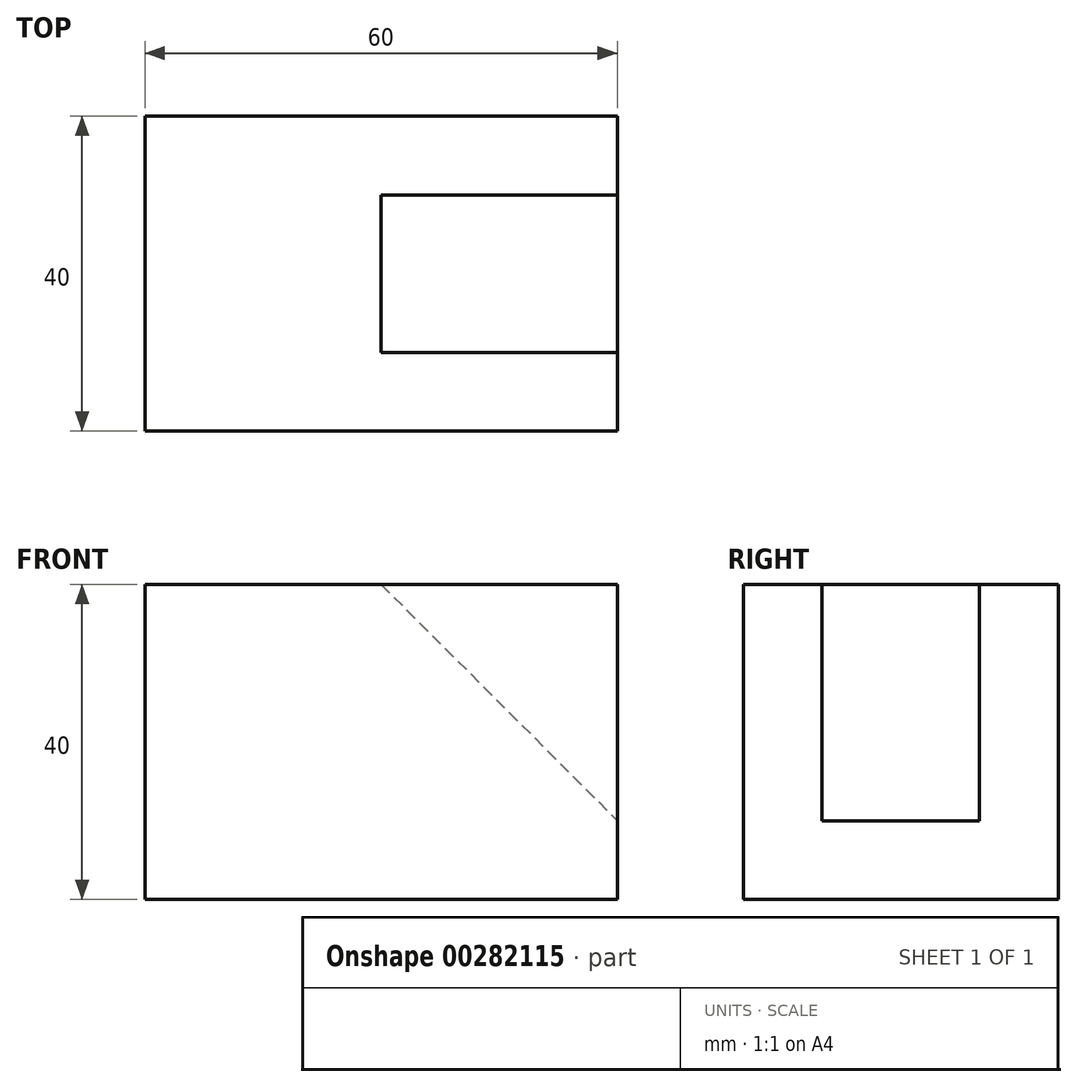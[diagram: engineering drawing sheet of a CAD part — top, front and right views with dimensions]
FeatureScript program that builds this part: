
annotation { "Feature Type Name" : "Feature", "Feature Type Description" : "" }
export const myFeature = defineFeature(function(context is Context, id is Id, definition is map)
    precondition{}
    {
        {
            var Q0;
            Q0=qCreatedBy(makeId("Front.planeOp"),FACE);
            var sketch = newSketch(context, id + "F0", { "sketchPlane" : qUnion([Q0])});
            skLineSegment(sketch, "E0", {"start": v(39.64, 0) * mm, "end": v(39.64, 10) * mm});
            skLineSegment(sketch, "E1", {"start": v(39.64, 10) * mm, "end": v(9.64, 40) * mm});
            skLineSegment(sketch, "E2", {"start": v(9.64, 40) * mm, "end": v(-20.36, 40) * mm});
            skLineSegment(sketch, "E3", {"start": v(-20.36, 40) * mm, "end": v(-20.36, 0) * mm});
            skLineSegment(sketch, "E4", {"start": v(-20.36, 0) * mm, "end": v(39.64, 0) * mm});
            skSolve(sketch);
        }
        {
            var Q0;
            Q0 = qSketchRegion(id + "F0", true);
            extrude(context, id + "F1", {"entities" : qUnion([Q0]), "oppositeDirection" : true, "depth" : 40 * mm});
        }
        {
            var Q0;
            Q0=makeQuery(id+"F1.opExtrude","SWEPT_FACE",FACE,{"disambiguationData":[OSD([sQuery(id+"F0.wireOp",EDGE,"E4")])]});
            var sketch = newSketch(context, id + "F2", { "sketchPlane" : qUnion([Q0])});
            skLineSegment(sketch, "E5", {"start": v(39.64, 0) * mm, "end": v(39.64, -10) * mm});
            skLineSegment(sketch, "E6", {"start": v(39.64, -10) * mm, "end": v(9.64, -10) * mm});
            skLineSegment(sketch, "E7", {"start": v(9.64, -10) * mm, "end": v(9.64, -30) * mm});
            skLineSegment(sketch, "E8", {"start": v(9.64, -30) * mm, "end": v(39.64, -30) * mm});
            skLineSegment(sketch, "E9", {"start": v(39.64, -30) * mm, "end": v(39.64, -40) * mm});
            skLineSegment(sketch, "E10", {"start": v(39.64, -40) * mm, "end": v(2.8, -40) * mm});
            skLineSegment(sketch, "E11", {"start": v(2.8, -40) * mm, "end": v(2.8, 0) * mm});
            skLineSegment(sketch, "E12", {"start": v(2.8, 0) * mm, "end": v(39.64, 0) * mm});
            skSolve(sketch);
        }
        {
            var Q0;
            Q0 = qSketchRegion(id + "F2", true);
            extrude(context, id + "F3", {"entities" : qUnion([Q0]), "operationType" : NewBodyOperationType.ADD, "oppositeDirection" : true, "depth" : 40 * mm});
        }
    });
